# Revit family: Mixer-Basin-Dorf Industrie1
name_source: partatom
category: Plumbing Fixtures
revit_build: Autodesk Revit 2014 (Build: 20131024_2115(x64)
units: mm (PartAtom-declared; Revit-internal decimal feet)

## types (3) — shared parameters
Assembly Code = D2020300
CW Connection = Yes
CWFU = 1.58
Connector Radius = 10 mm  [stored 0.0328084 ft]
HW Connection = Yes
HWFU = 1.58
Height_ANZRS = 154 mm
Length_ANZRS = 176 mm
Manufacturer = GWA Bathrooms & Kitchens
Material_ANZRS = Metal-Chrome-Caroma
ModifiedIssue_ANZRS = 20150504 $
Type Comments = Dorf Industrie Basin Mixer
URL = http://specify.caroma.com.au
Vent Connection = No
WELSRating_ANZRS = WELS 5 star rated, 6L/min
Waste Connection = No
Width_ANZRS = 160 mm
zero-valued in all types: Cost, Default Elevation

## per-type parameters (varying)
| type | Handle | Model |
| Black Handles | Metal-Powdercoat-Black-Caroma | 6103.045A |
| Red Handles | Metal-Powdercoat-Red-Caroma | 6101.045A |
| White Handles | Metal-Powdercoat-White-Caroma | 6102.045A |

note: [stored X ft] marks values corroborated as IEEE doubles in the binary element streams (Revit-internal decimal feet)

## geometry (parser evidence)
native form markers: Blend x2, Sweep x2
no freeform markers — native parametric forms only
